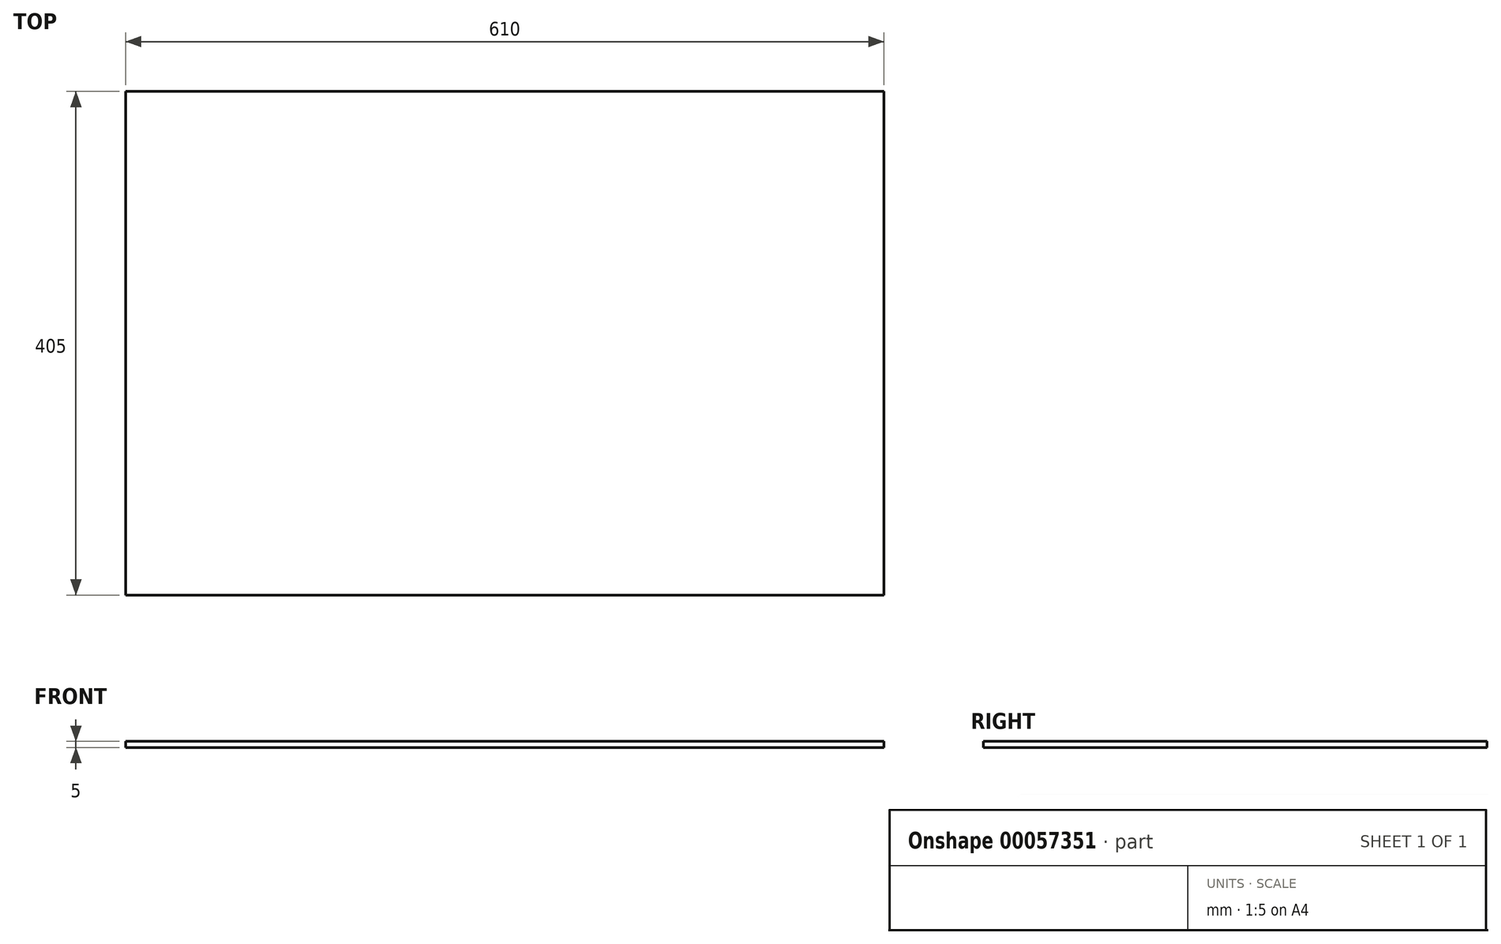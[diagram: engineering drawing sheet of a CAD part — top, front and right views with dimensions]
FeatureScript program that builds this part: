
annotation { "Feature Type Name" : "Feature", "Feature Type Description" : "" }
export const myFeature = defineFeature(function(context is Context, id is Id, definition is map)
    precondition{}
    {
        {
            var Q0;
            Q0=qCreatedBy(makeId("Top.planeOp"),FACE);
            var sketch = newSketch(context, id + "F0", { "sketchPlane" : qUnion([Q0])});
            skLineSegment(sketch, "E0.bottom", {"start": v(0, 0) * mm, "end": v(610, 0) * mm});
            skLineSegment(sketch, "E0.top", {"start": v(0, 405) * mm, "end": v(610, 405) * mm});
            skLineSegment(sketch, "E0.left", {"start": v(0, 0) * mm, "end": v(0, 405) * mm});
            skLineSegment(sketch, "E0.right", {"start": v(610, 0) * mm, "end": v(610, 405) * mm});
            skSolve(sketch);
        }
        {
            var Q0;
            Q0=makeQuery(id+"F0.imprint","IMPRINT",FACE,{"disambiguationData":[TD([[makeQuery(id+"F0.imprint","IMPRINT",EDGE,{"derivedFrom":sQuery(id+"F0.wireOp",EDGE,"E0.bottom")}),1.0]])]});
            extrude(context, id + "F1", {"entities" : qUnion([Q0]), "depth" : 5 * mm});
        }
    });
